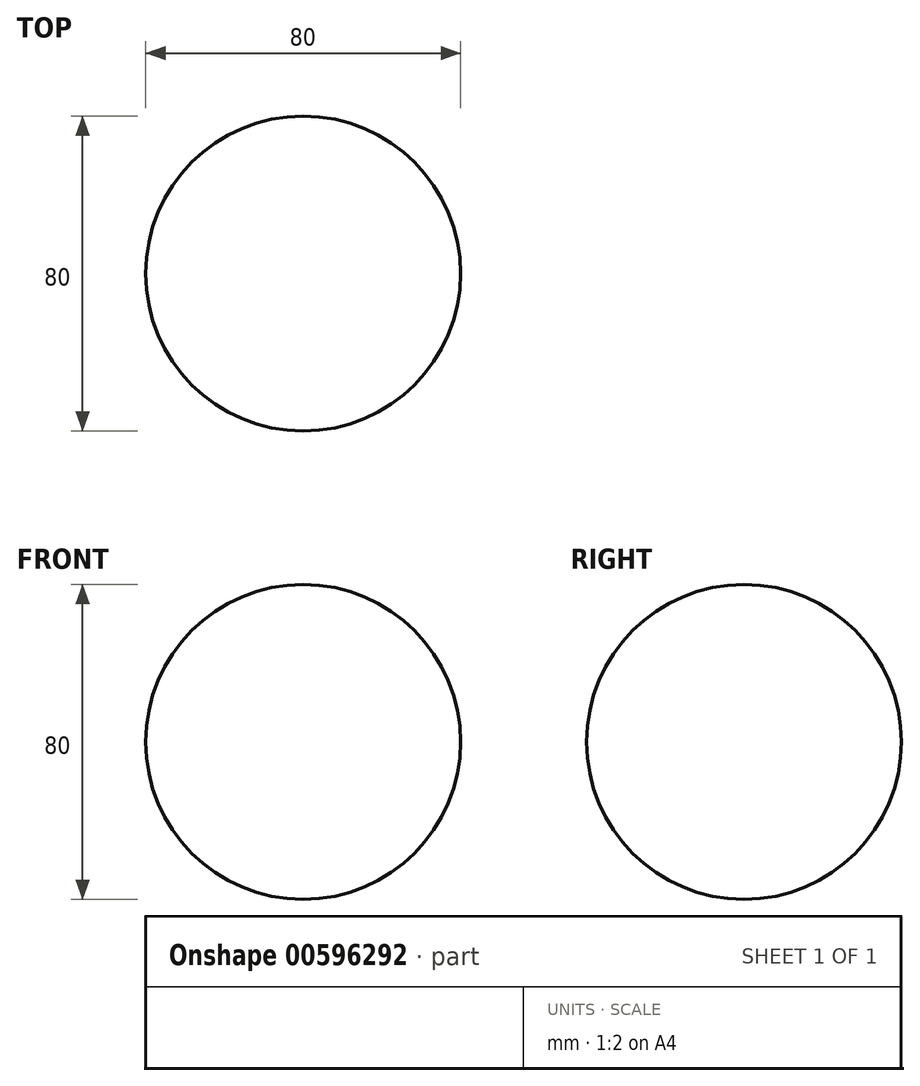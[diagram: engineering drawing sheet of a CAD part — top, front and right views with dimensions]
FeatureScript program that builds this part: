
annotation { "Feature Type Name" : "Feature", "Feature Type Description" : "" }
export const myFeature = defineFeature(function(context is Context, id is Id, definition is map)
    precondition{}
    {
        {
            var Q0;
            Q0=qCreatedBy(makeId("Front.planeOp"),FACE);
            var sketch = newSketch(context, id + "F0", { "sketchPlane" : qUnion([Q0])});
            skArc(sketch, "E0", {"start": v(0, -40) * mm, "mid": v(40, 0) * mm, "end": v(0, 40) * mm});
            skLineSegment(sketch, "E1", {"start": v(0, 40) * mm, "end": v(0, -40) * mm});
            skSolve(sketch);
        }
        {
            var Q0;
            Q0=qCreatedBy(makeId("Front.planeOp"),FACE);
            var sketch = newSketch(context, id + "F1", { "sketchPlane" : qUnion([Q0])});
            skLineSegment(sketch, "E2", {"start": v(0, 0) * mm, "end": v(0, 46.22) * mm});
            skSolve(sketch);
        }
        {
            var Q0;
            Q0 = qSketchRegion(id + "F0", true);
            var Q1;
            Q1=sQuery(id+"F1.wireOp",EDGE,"E2");
            revolve(context, id + "F2", {"entities" : qUnion([Q0]), "axis" : qUnion([Q1]), "revolveType" : RevolveType.FULL});
        }
    });
